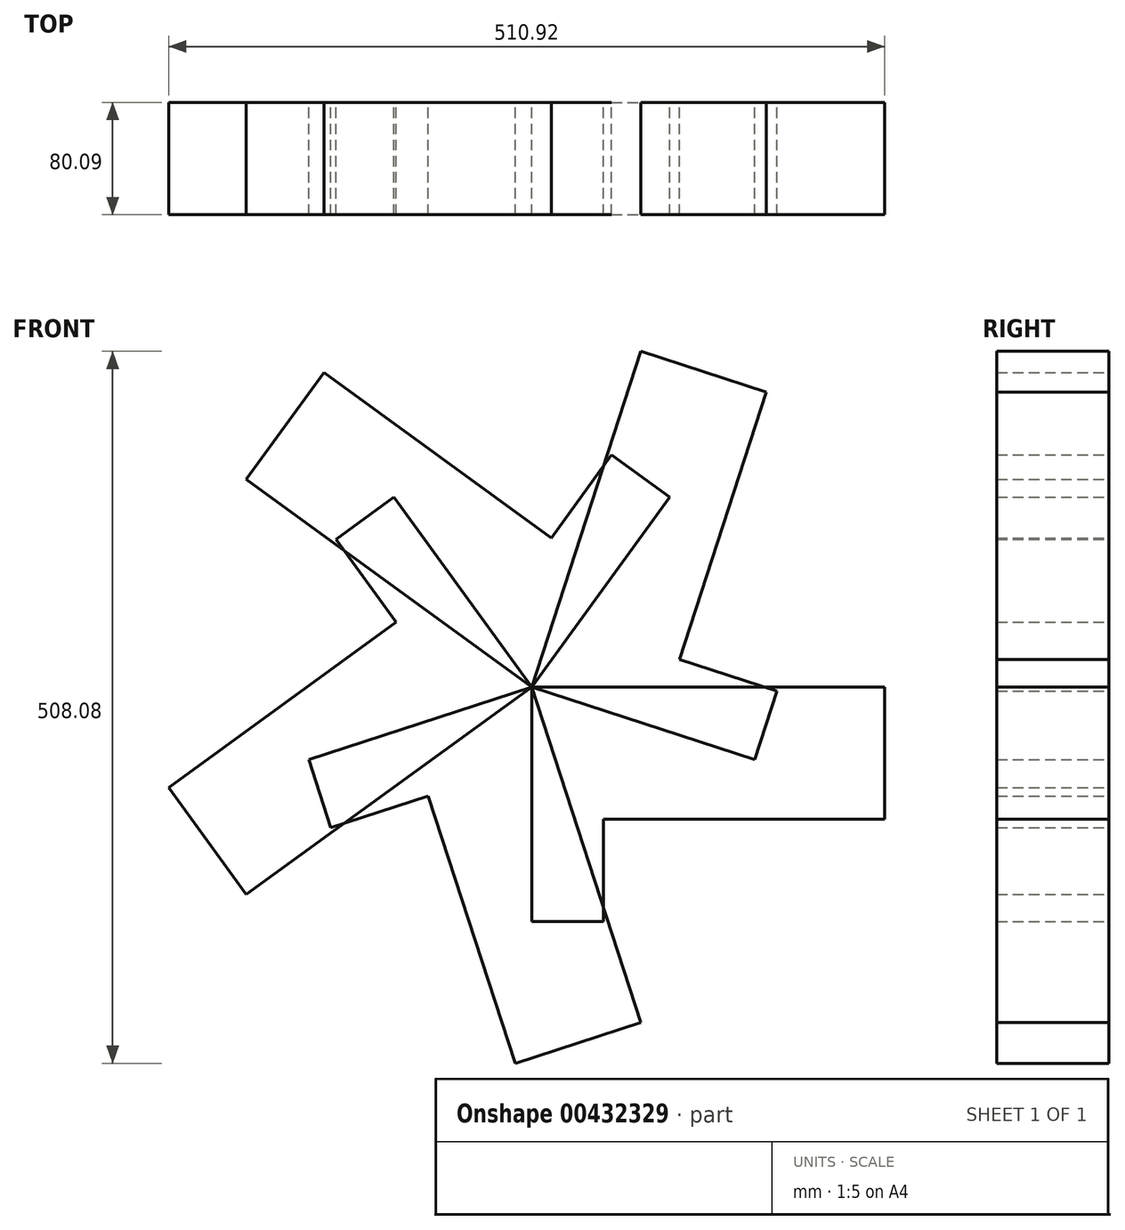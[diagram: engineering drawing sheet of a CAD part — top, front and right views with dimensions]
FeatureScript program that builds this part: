
annotation { "Feature Type Name" : "Feature", "Feature Type Description" : "" }
export const myFeature = defineFeature(function(context is Context, id is Id, definition is map)
    precondition{}
    {
        {
            var Q0;
            Q0=qCreatedBy(makeId("Front.planeOp"),FACE);
            var sketch = newSketch(context, id + "F0", { "sketchPlane" : qUnion([Q0])});
            skLineSegment(sketch, "E0", {"start": v(-152.99, -73.1) * mm, "end": v(-152.99, 94.27) * mm});
            skLineSegment(sketch, "E1", {"start": v(-152.99, 94.27) * mm, "end": v(98.8, 94.27) * mm});
            skLineSegment(sketch, "E2", {"start": v(98.8, 94.27) * mm, "end": v(98.8, 0) * mm});
            skLineSegment(sketch, "E3", {"start": v(98.8, 0) * mm, "end": v(-101.78, 0) * mm});
            skLineSegment(sketch, "E4", {"start": v(-101.78, 0) * mm, "end": v(-101.78, -73.1) * mm});
            skLineSegment(sketch, "E5", {"start": v(-101.78, -73.1) * mm, "end": v(-152.99, -73.1) * mm});
            skSolve(sketch);
        }
        {
            var Q0;
            Q0=makeQuery(id+"F0.imprint","IMPRINT",FACE,{"disambiguationData":[TD([[makeQuery(id+"F0.imprint","IMPRINT",EDGE,{"derivedFrom":sQuery(id+"F0.wireOp",EDGE,"E0")}),-1.0]])]});
            extrude(context, id + "F1", {"entities" : qUnion([Q0]), "depth" : 80.1 * mm});
        }
        {
            var Q0;
            Q0=makeQuery(id+"F1.opExtrude","SWEPT_BODY",BODY,{"disambiguationData":[OSD([sQuery(id+"F0.wireOp",EDGE,"E0"),sQuery(id+"F0.wireOp",EDGE,"E1"),sQuery(id+"F0.wireOp",EDGE,"E2"),sQuery(id+"F0.wireOp",EDGE,"E3"),sQuery(id+"F0.wireOp",EDGE,"E4"),sQuery(id+"F0.wireOp",EDGE,"E5")])]});
            var Q1;
            Q1=makeQuery(id+"F1.opExtrude","SWEPT_EDGE",EDGE,{"disambiguationData":[OSD([sQuery(id+"F0.wireOp",EDGE,"E0"),sQuery(id+"F0.wireOp",EDGE,"E1")])]});
            circularPattern(context, id + "F2", {"entities" : qUnion([Q0]), "axis" : qUnion([Q1]), "angle" : 360 * degree, "instanceCount" : 5, "equalSpace" : true});
        }
    });
